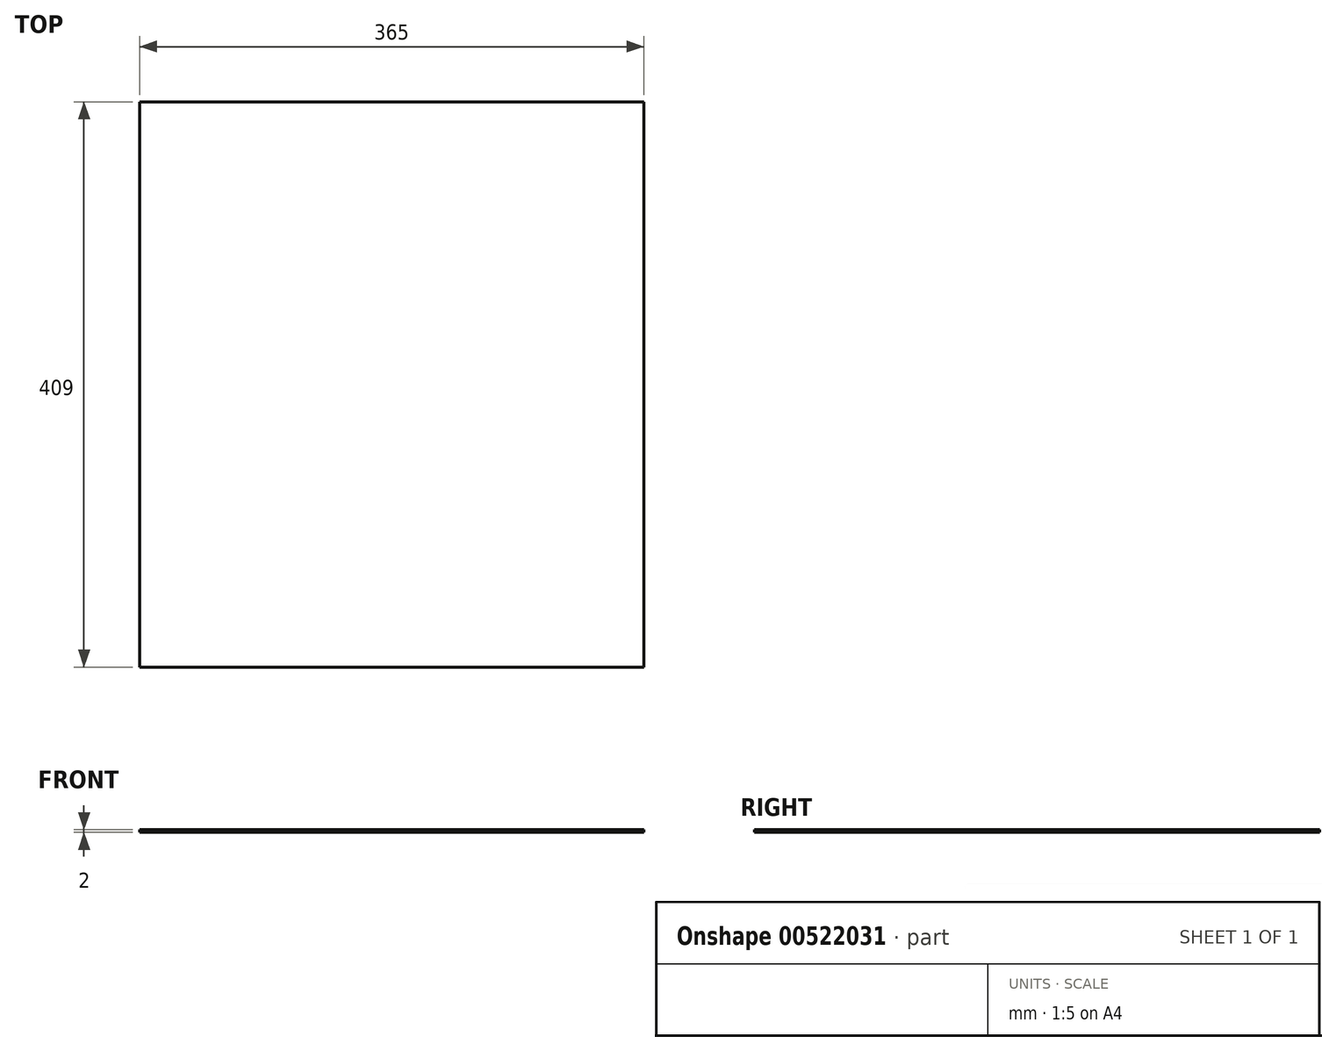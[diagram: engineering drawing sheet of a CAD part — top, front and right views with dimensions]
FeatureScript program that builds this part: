
annotation { "Feature Type Name" : "Feature", "Feature Type Description" : "" }
export const myFeature = defineFeature(function(context is Context, id is Id, definition is map)
    precondition{}
    {
        {
            var Q0;
            Q0=qCreatedBy(makeId("Top.planeOp"),FACE);
            var sketch = newSketch(context, id + "F0", { "sketchPlane" : qUnion([Q0])});
            skLineSegment(sketch, "E0.bottom", {"start": v(0, 0) * mm, "end": v(365, 0) * mm});
            skLineSegment(sketch, "E0.top", {"start": v(0, 409) * mm, "end": v(365, 409) * mm});
            skLineSegment(sketch, "E0.left", {"start": v(0, 0) * mm, "end": v(0, 409) * mm});
            skLineSegment(sketch, "E0.right", {"start": v(365, 0) * mm, "end": v(365, 409) * mm});
            skSolve(sketch);
        }
        {
            var Q0;
            Q0=makeQuery(id+"F0.imprint","IMPRINT",FACE,{"disambiguationData":[TD([[makeQuery(id+"F0.imprint","IMPRINT",EDGE,{"derivedFrom":sQuery(id+"F0.wireOp",EDGE,"E0.bottom")}),1.0]])]});
            extrude(context, id + "F1", {"entities" : qUnion([Q0]), "depth" : 2 * mm, "offsetDistance" : 25 * mm});
        }
    });
